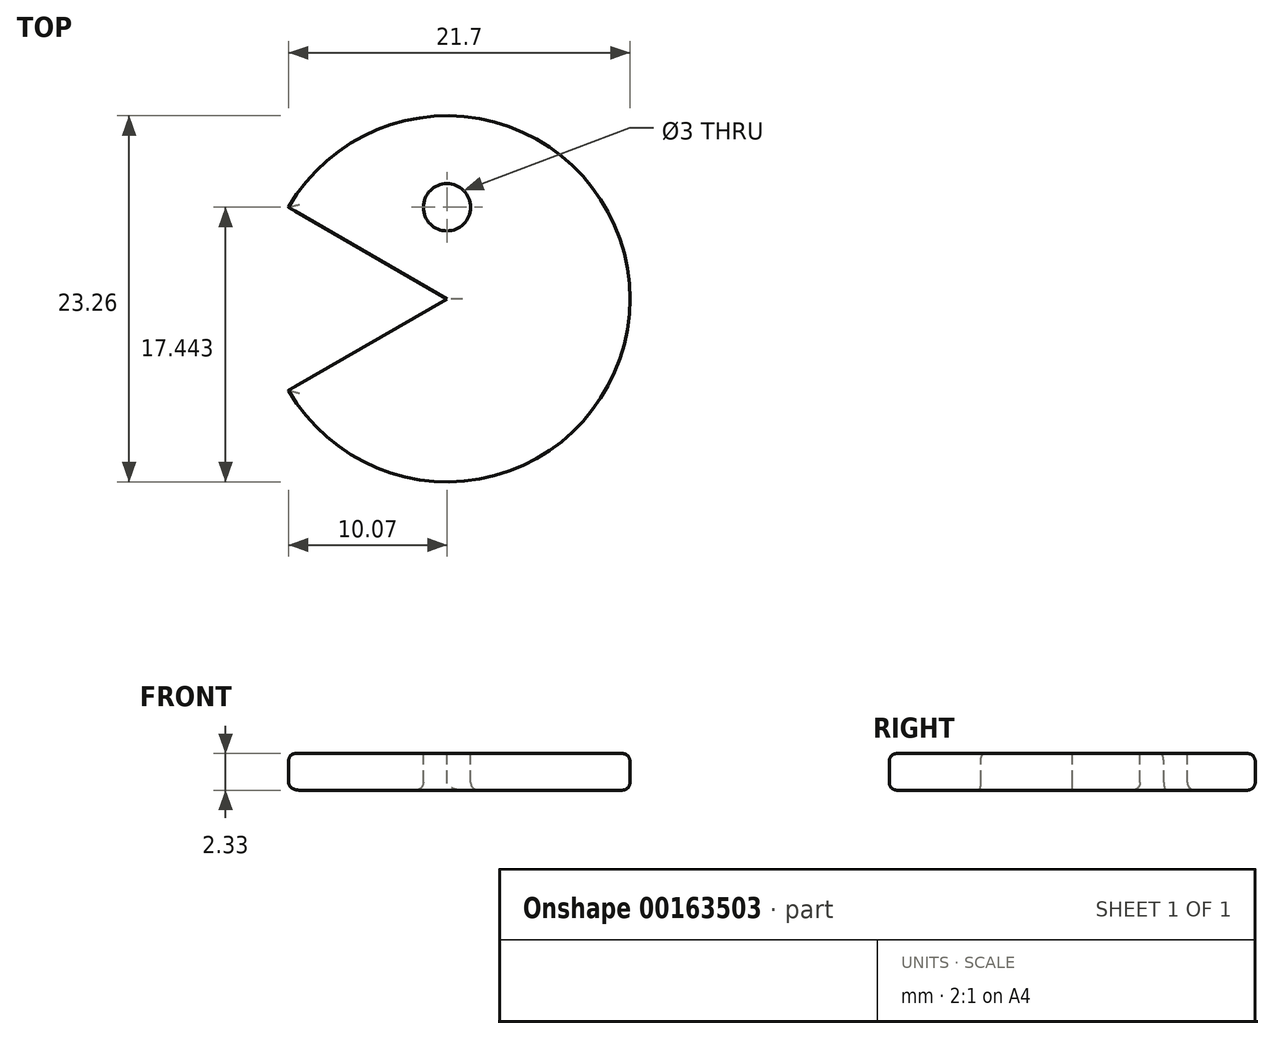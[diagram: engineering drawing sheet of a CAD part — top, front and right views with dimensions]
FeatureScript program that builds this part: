
annotation { "Feature Type Name" : "Feature", "Feature Type Description" : "" }
export const myFeature = defineFeature(function(context is Context, id is Id, definition is map)
    precondition{}
    {
        {
            var Q0;
            Q0=qCreatedBy(makeId("Top.planeOp"),FACE);
            var sketch = newSketch(context, id + "F0", { "sketchPlane" : qUnion([Q0])});
            skCircle(sketch, "E0", {"center": v(0, 0) * mm, "radius": 11.62 * mm});
            skSolve(sketch);
        }
        {
            var Q0;
            Q0 = qSketchRegion(id + "F0", true);
            extrude(context, id + "F1", {"entities" : qUnion([Q0]), "depth" : 2.33 * mm});
        }
        {
            var Q0;
            Q0=makeQuery(id+"F1.opExtrude","CAP_FACE",FACE,{"disambiguationData":[OSD([sQuery(id+"F0.wireOp",EDGE,"E0")])],"isStart":false});
            var sketch = newSketch(context, id + "F2", { "sketchPlane" : qUnion([Q0])});
            skLineSegment(sketch, "E1", {"start": v(0, 0) * mm, "end": v(-10.07, -5.81) * mm});
            skLineSegment(sketch, "E2", {"start": v(0, 0) * mm, "end": v(-10.07, 5.81) * mm});
            skSolve(sketch);
        }
        {
            var Q0;
            {var subQ0=sQuery(id+"F2.wireOp",EDGE,"E1");Q0=makeQuery(id+"F2.imprint","IMPRINT",FACE,{"disambiguationData":[TD([[makeQuery(id+"F2.imprint","IMPRINT",EDGE,{"derivedFrom":subQ0}),-1.0]])]});}
            extrude(context, id + "F3", {"entities" : qUnion([Q0]), "operationType" : NewBodyOperationType.REMOVE, "endBound" : BoundingType.THROUGH_ALL, "oppositeDirection" : true, "depth" : 25 * mm});
        }
        {
            var Q0;
            Q0=makeQuery(id+"F1.opExtrude","CAP_FACE",FACE,{"disambiguationData":[OSD([sQuery(id+"F0.wireOp",EDGE,"E0")])],"isStart":false});
            var sketch = newSketch(context, id + "F4", { "sketchPlane" : qUnion([Q0])});
            skCircle(sketch, "E3", {"center": v(0, 5.81) * mm, "radius": 1.5 * mm});
            skLineSegment(sketch, "E4", {"start": v(0, 11.62) * mm, "end": v(0, 0) * mm, "construction": true});
            skSolve(sketch);
        }
        {
            var Q0;
            Q0=makeQuery(id+"F4.imprint","IMPRINT",FACE,{"disambiguationData":[TD([[makeQuery(id+"F4.imprint","IMPRINT",EDGE,{"derivedFrom":sQuery(id+"F4.wireOp",EDGE,"E3")}),1.0]])]});
            extrude(context, id + "F5", {"entities" : qUnion([Q0]), "operationType" : NewBodyOperationType.REMOVE, "endBound" : BoundingType.THROUGH_ALL, "oppositeDirection" : true, "depth" : 25 * mm});
        }
        {
            var Q0;
            Q0=makeQuery(id+"F1.opExtrude","CAP_EDGE",EDGE,{"disambiguationData":[OSD([sQuery(id+"F0.wireOp",EDGE,"E0")])],"isStart":false});
            var Q1;
            Q1=makeQuery(id+"F1.opExtrude","CAP_EDGE",EDGE,{"disambiguationData":[OSD([sQuery(id+"F0.wireOp",EDGE,"E0")])],"isStart":true});
            var Q2;
            Q2=makeQuery(id+"F3.boolean.opBoolean","COPY",EDGE,{"derivedFrom":makeQuery(id+"F3.opExtrude","CAP_EDGE",EDGE,{"disambiguationData":[OSD([sQuery(id+"F2.wireOp",EDGE,"E1")])],"isStart":true})});
            var Q3;
            Q3=makeQuery(id+"F3.boolean.opBoolean","COPY",EDGE,{"derivedFrom":makeQuery(id+"F3.opExtrude","CAP_EDGE",EDGE,{"disambiguationData":[OSD([sQuery(id+"F2.wireOp",EDGE,"E2")])],"isStart":true})});
            var Q4;
            Q4=makeQuery(id+"F3.boolean.opBoolean","INTERSECT",EDGE,{"derivedFrom":[makeQuery(id+"F1.opExtrude","CAP_FACE",FACE,{"disambiguationData":[OSD([sQuery(id+"F0.wireOp",EDGE,"E0")])],"isStart":true}),makeQuery(id+"F3.opExtrude","SWEPT_FACE",FACE,{"disambiguationData":[OSD([sQuery(id+"F2.wireOp",EDGE,"E1")])]})]});
            var Q5;
            Q5=makeQuery(id+"F3.boolean.opBoolean","INTERSECT",EDGE,{"derivedFrom":[makeQuery(id+"F1.opExtrude","CAP_FACE",FACE,{"disambiguationData":[OSD([sQuery(id+"F0.wireOp",EDGE,"E0")])],"isStart":true}),makeQuery(id+"F3.opExtrude","SWEPT_FACE",FACE,{"disambiguationData":[OSD([sQuery(id+"F2.wireOp",EDGE,"E2")])]})]});
            var Q6;
            Q6=makeQuery(id+"F5.boolean.opBoolean","INTERSECT",EDGE,{"derivedFrom":[makeQuery(id+"F1.opExtrude","CAP_FACE",FACE,{"disambiguationData":[OSD([sQuery(id+"F0.wireOp",EDGE,"E0")])],"isStart":true}),makeQuery(id+"F5.opExtrude","SWEPT_FACE",FACE,{"disambiguationData":[OSD([sQuery(id+"F4.wireOp",EDGE,"E3")])]})]});
            var Q7;
            Q7=makeQuery(id+"F5.boolean.opBoolean","COPY",EDGE,{"derivedFrom":makeQuery(id+"F5.opExtrude","CAP_EDGE",EDGE,{"disambiguationData":[OSD([sQuery(id+"F4.wireOp",EDGE,"E3")])],"isStart":true})});
            fillet(context, id + "F6", {"entities" : qUnion([Q0, Q1, Q2, Q3, Q4, Q5, Q6, Q7]), "radius" : 0.5 * mm, "tangentPropagation" : true, "allowEdgeOverflow" : false});
        }
    });
